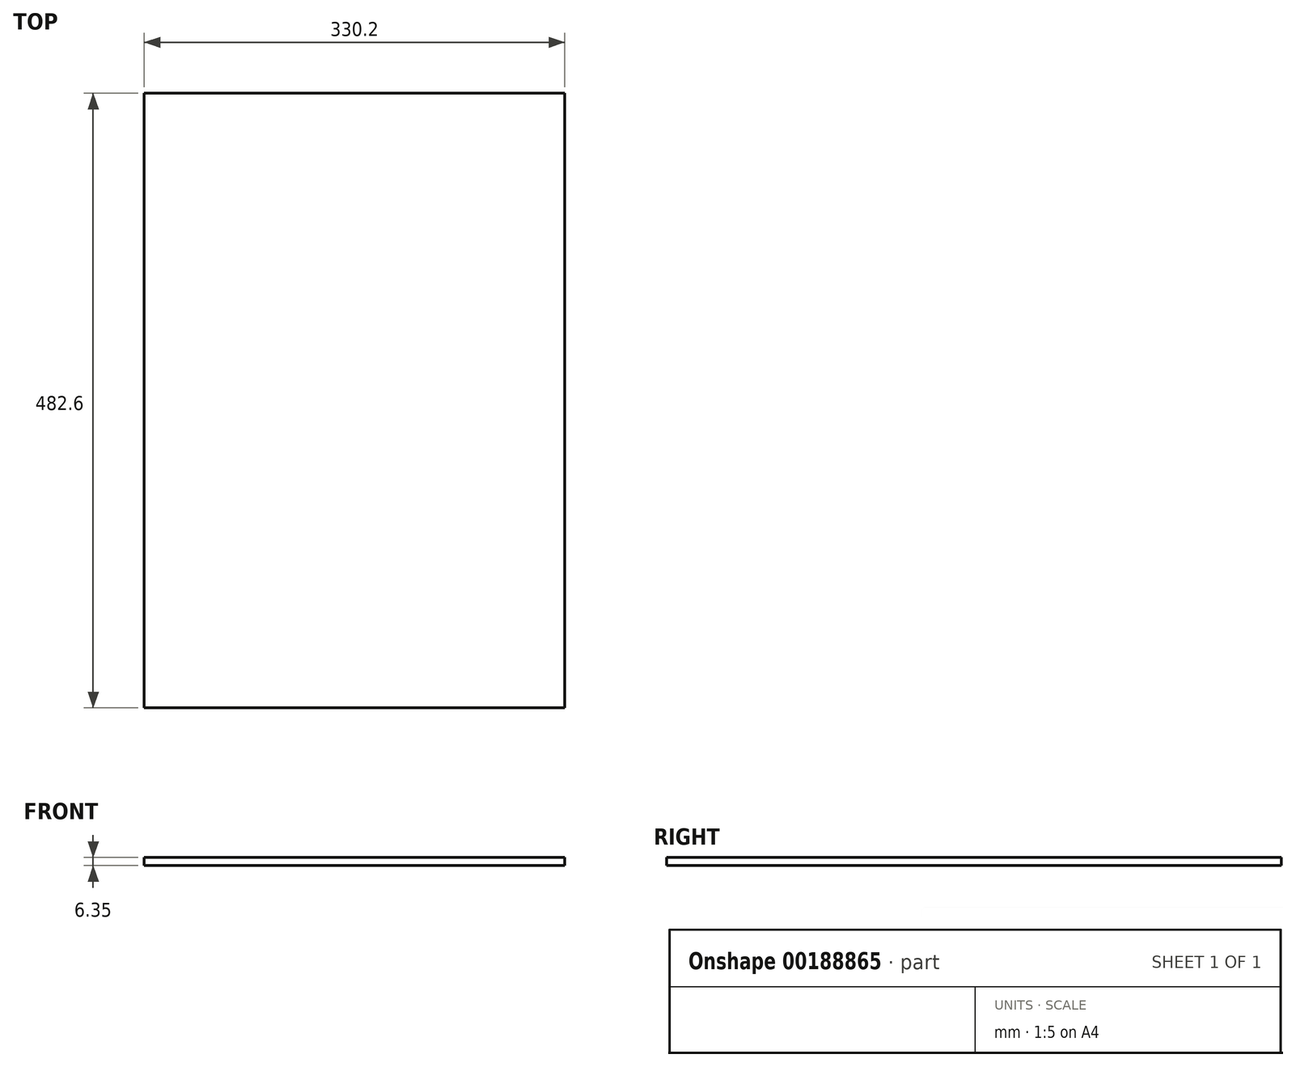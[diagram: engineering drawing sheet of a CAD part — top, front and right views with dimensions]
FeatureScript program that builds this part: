
annotation { "Feature Type Name" : "Feature", "Feature Type Description" : "" }
export const myFeature = defineFeature(function(context is Context, id is Id, definition is map)
    precondition{}
    {
        {
            var Q0;
            Q0=qCreatedBy(makeId("Top.planeOp"),FACE);
            var sketch = newSketch(context, id + "F0", { "sketchPlane" : qUnion([Q0])});
            skLineSegment(sketch, "E0.bottom", {"start": v(165.1, -241.3) * mm, "end": v(-165.1, -241.3) * mm});
            skLineSegment(sketch, "E0.top", {"start": v(165.1, 241.3) * mm, "end": v(-165.1, 241.3) * mm});
            skLineSegment(sketch, "E0.left", {"start": v(165.1, -241.3) * mm, "end": v(165.1, 241.3) * mm});
            skLineSegment(sketch, "E0.right", {"start": v(-165.1, -241.3) * mm, "end": v(-165.1, 241.3) * mm});
            skPoint(sketch, "E0.middle", {"position": v(0, 0) * mm});
            skSolve(sketch);
        }
        {
            var Q0;
            Q0 = qSketchRegion(id + "F0", true);
            extrude(context, id + "F1", {"entities" : qUnion([Q0]), "depth" : 6.35 * mm, "offsetDistance" : 25.4 * mm});
        }
    });
